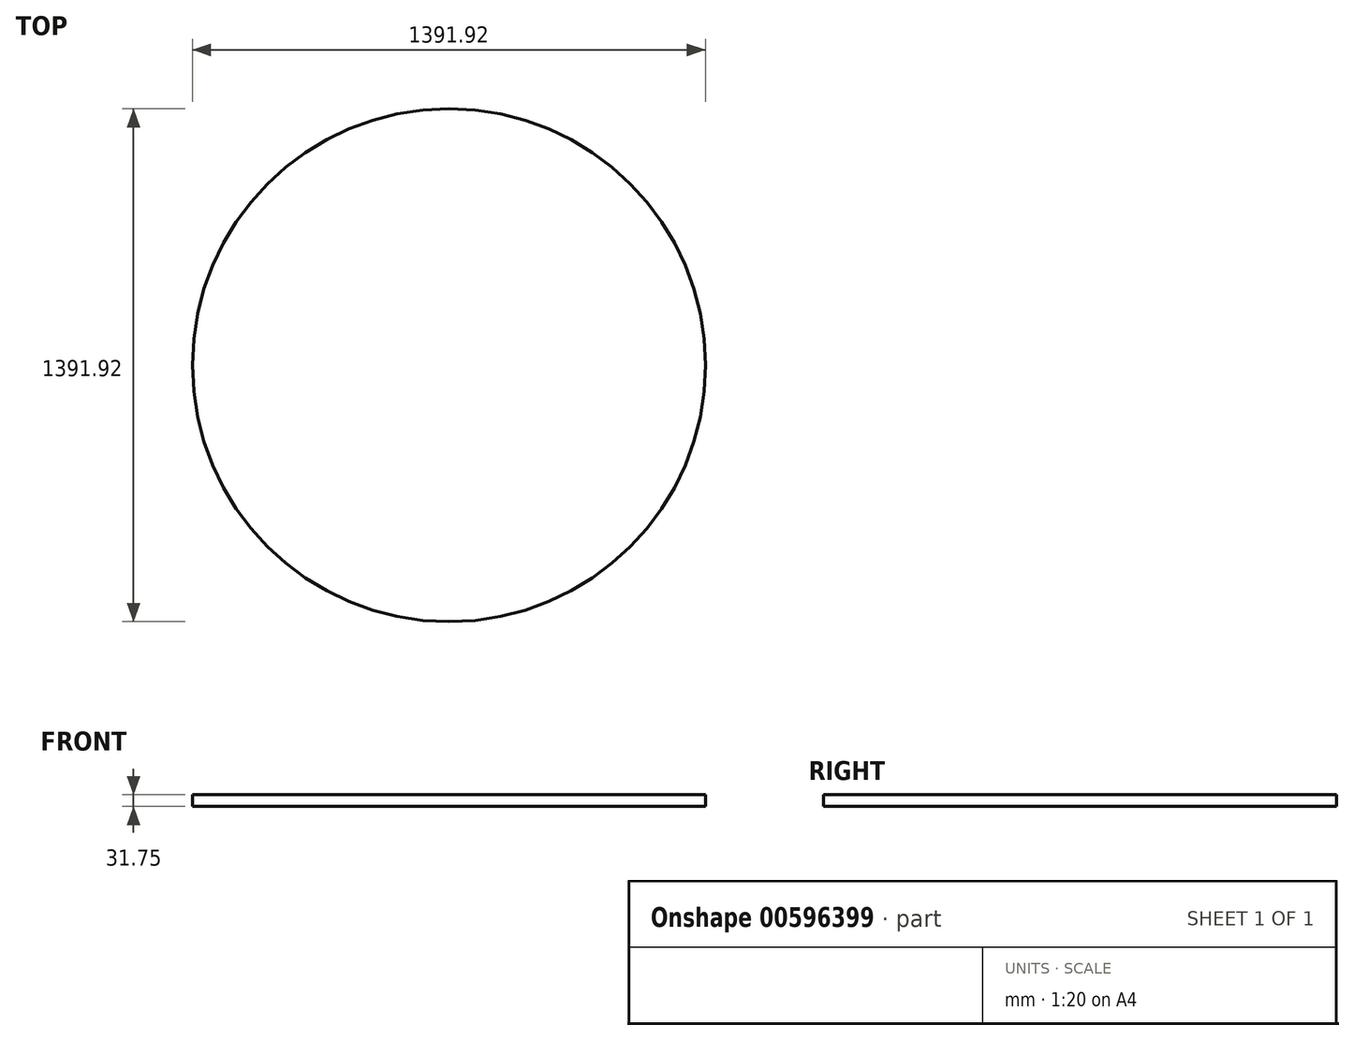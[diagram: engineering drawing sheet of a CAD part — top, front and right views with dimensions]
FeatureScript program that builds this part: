
annotation { "Feature Type Name" : "Feature", "Feature Type Description" : "" }
export const myFeature = defineFeature(function(context is Context, id is Id, definition is map)
    precondition{}
    {
        {
            var Q0;
            Q0=qCreatedBy(makeId("Top.planeOp"),FACE);
            var sketch = newSketch(context, id + "F0", { "sketchPlane" : qUnion([Q0])});
            skCircle(sketch, "E0", {"center": v(0, 0) * mm, "radius": 695.96 * mm});
            skCircle(sketch, "E1", {"center": v(0, 0) * mm, "radius": 675.64 * mm});
            skCircle(sketch, "E2", {"center": v(0, 0) * mm, "radius": 228.6 * mm});
            skCircle(sketch, "E3", {"center": v(0, 0) * mm, "radius": 199.24 * mm});
            skCircle(sketch, "E4", {"center": v(0, 0) * mm, "radius": 152.4 * mm});
            skCircle(sketch, "E5", {"center": v(0, 0) * mm, "radius": 101.6 * mm});
            skSolve(sketch);
        }
        {
            var Q0;
            Q0=makeQuery(id+"F0.imprint","IMPRINT",FACE,{"disambiguationData":[TD([[makeQuery(id+"F0.imprint","IMPRINT",EDGE,{"derivedFrom":sQuery(id+"F0.wireOp",EDGE,"E0")}),1.0]])]});
            var Q1;
            Q1=makeQuery(id+"F0.imprint","IMPRINT",FACE,{"disambiguationData":[TD([[makeQuery(id+"F0.imprint","IMPRINT",EDGE,{"derivedFrom":sQuery(id+"F0.wireOp",EDGE,"E1")}),1.0]])]});
            var Q2;
            Q2=makeQuery(id+"F0.imprint","IMPRINT",FACE,{"disambiguationData":[TD([[makeQuery(id+"F0.imprint","IMPRINT",EDGE,{"derivedFrom":sQuery(id+"F0.wireOp",EDGE,"E2")}),1.0]])]});
            var Q3;
            Q3=makeQuery(id+"F0.imprint","IMPRINT",FACE,{"disambiguationData":[TD([[makeQuery(id+"F0.imprint","IMPRINT",EDGE,{"derivedFrom":sQuery(id+"F0.wireOp",EDGE,"E3")}),1.0]])]});
            var Q4;
            Q4=makeQuery(id+"F0.imprint","IMPRINT",FACE,{"disambiguationData":[TD([[makeQuery(id+"F0.imprint","IMPRINT",EDGE,{"derivedFrom":sQuery(id+"F0.wireOp",EDGE,"E4")}),1.0]])]});
            var Q5;
            Q5=makeQuery(id+"F0.imprint","IMPRINT",FACE,{"disambiguationData":[TD([[makeQuery(id+"F0.imprint","IMPRINT",EDGE,{"derivedFrom":sQuery(id+"F0.wireOp",EDGE,"E5")}),1.0]])]});
            extrude(context, id + "F1", {"entities" : qUnion([Q0, Q1, Q2, Q3, Q4, Q5]), "depth" : 31.75 * mm, "offsetDistance" : 25.4 * mm});
        }
        {
            var Q0;
            Q0=sQuery(id+"F0.wireOp",EDGE,"E0");
            var Q1;
            Q1=sQuery(id+"F0.wireOp",EDGE,"E1");
            extrude(context, id + "F2", {"bodyType" : ToolBodyType.SURFACE, "surfaceEntities" : qUnion([Q0, Q1]), "depth" : 349.25 * mm, "offsetDistance" : 25.4 * mm});
        }
    });
